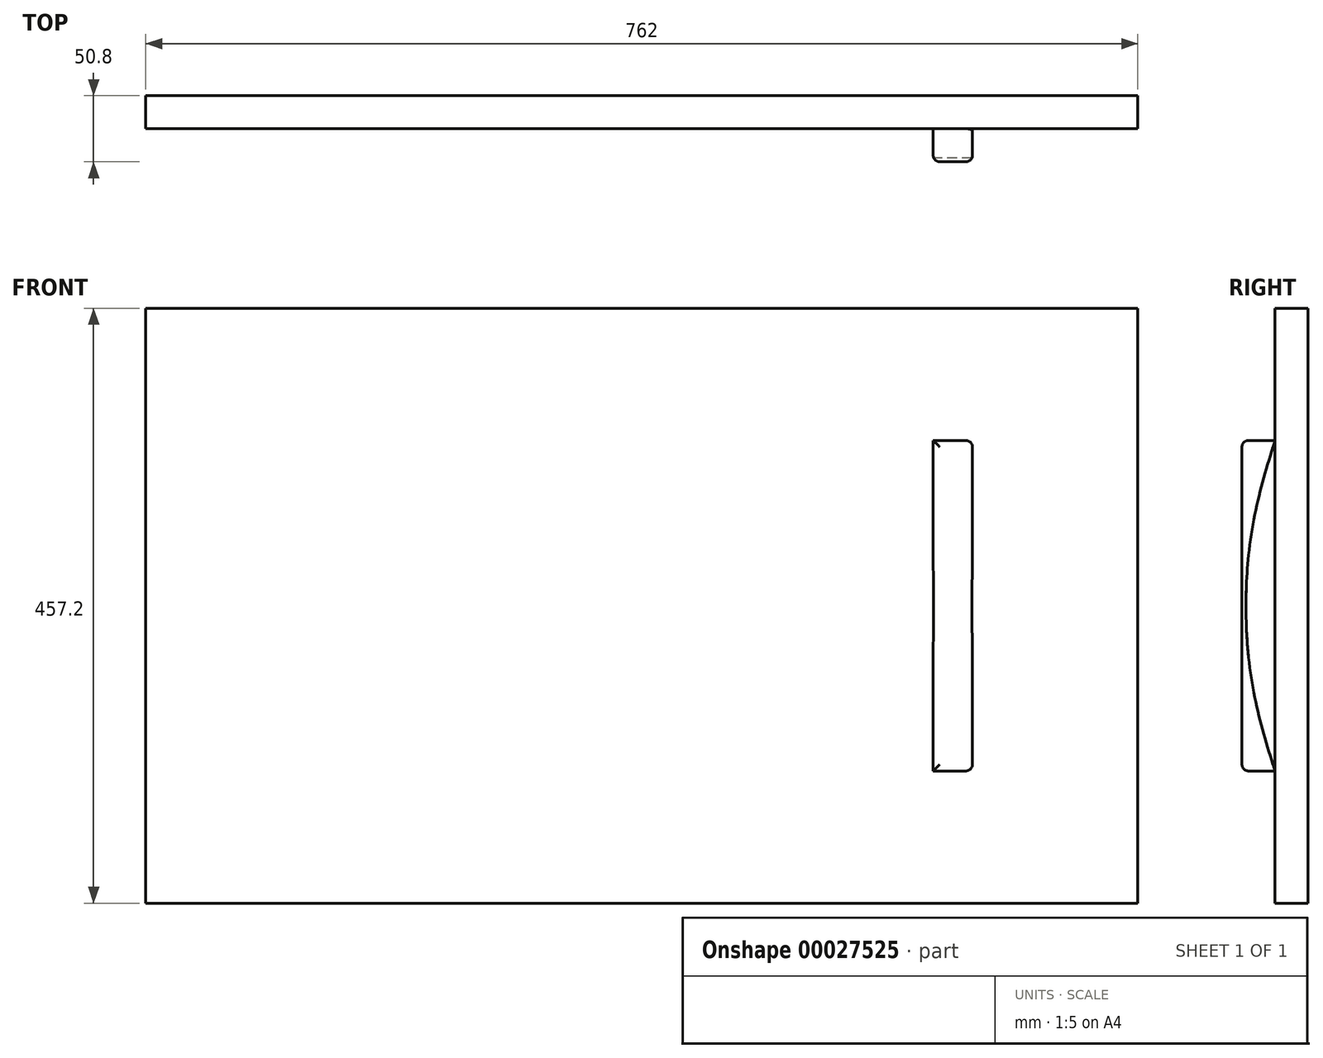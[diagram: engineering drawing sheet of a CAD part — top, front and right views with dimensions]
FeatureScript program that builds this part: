
annotation { "Feature Type Name" : "Feature", "Feature Type Description" : "" }
export const myFeature = defineFeature(function(context is Context, id is Id, definition is map)
    precondition{}
    {
        {
            var Q0;
            Q0=qCreatedBy(makeId("Front.planeOp"),FACE);
            var sketch = newSketch(context, id + "F0", { "sketchPlane" : qUnion([Q0])});
            skLineSegment(sketch, "E0.bottom", {"start": v(-381, 158.23) * mm, "end": v(381, 158.23) * mm});
            skLineSegment(sketch, "E0.top", {"start": v(-381, -298.97) * mm, "end": v(381, -298.97) * mm});
            skLineSegment(sketch, "E0.left", {"start": v(-381, 158.23) * mm, "end": v(-381, -298.97) * mm});
            skLineSegment(sketch, "E0.right", {"start": v(381, 158.23) * mm, "end": v(381, -298.97) * mm});
            skLineSegment(sketch, "E1", {"start": v(-430.92, -70.37) * mm, "end": v(506.87, -70.37) * mm, "construction": true});
            skLineSegment(sketch, "E2.bottom", {"start": v(223.82, 56.63) * mm, "end": v(254, 56.63) * mm});
            skLineSegment(sketch, "E2.top", {"start": v(223.82, -197.37) * mm, "end": v(254, -197.37) * mm});
            skLineSegment(sketch, "E2.left", {"start": v(223.82, 56.63) * mm, "end": v(223.82, -197.37) * mm});
            skLineSegment(sketch, "E2.right", {"start": v(254, 56.63) * mm, "end": v(254, -197.37) * mm});
            skSolve(sketch);
        }
        {
            var Q0;
            Q0=makeQuery(id+"F0.imprint","IMPRINT",FACE,{"disambiguationData":[TD([[makeQuery(id+"F0.imprint","IMPRINT",EDGE,{"derivedFrom":sQuery(id+"F0.wireOp",EDGE,"E2.bottom")}),-1.0]])]});
            extrude(context, id + "F1", {"entities" : qUnion([Q0]), "depth" : 50.8 * mm});
        }
        {
            var Q0;
            Q0 = qSketchRegion(id + "F0", true);
            extrude(context, id + "F2", {"entities" : qUnion([Q0]), "operationType" : NewBodyOperationType.ADD, "depth" : 25.4 * mm});
        }
        {
            var Q0;
            Q0=makeQuery(id+"F1.opExtrude","SWEPT_FACE",FACE,{"disambiguationData":[OSD([sQuery(id+"F0.wireOp",EDGE,"E2.right")])]});
            var sketch = newSketch(context, id + "F3", { "sketchPlane" : qUnion([Q0])});
            skLineSegment(sketch, "E3", {"start": v(-25.4, 56.63) * mm, "end": v(-25.4, -197.37) * mm});
            skFitSpline(sketch, "E4", {"points": [v(-25.4, 56.63) * mm, v(-44.3, -19.96) * mm, v(-44.3, -121.56) * mm, v(-25.4, -197.37) * mm], "startDerivative": vector(-70.1, -226.7) * mm, "endDerivative": vector(70.46, -225.23) * mm});
            skSolve(sketch);
        }
        {
            var Q0;
            Q0=makeQuery(id+"F3.imprint","IMPRINT",FACE,{"disambiguationData":[TD([[makeQuery(id+"F3.imprint","IMPRINT",EDGE,{"derivedFrom":sQuery(id+"F3.wireOp",EDGE,"392769a1-0da2-420d-8c07-b7950d6b351a")}),1.0]])]});
            var Q1;
            Q1=makeQuery(id+"F3.imprint","IMPRINT",FACE,{"disambiguationData":[TD([[makeQuery(id+"F3.imprint","IMPRINT",EDGE,{"derivedFrom":sQuery(id+"F3.wireOp",EDGE,"E3")}),-1.0]])]});
            extrude(context, id + "F4", {"entities" : qUnion([Q0, Q1]), "operationType" : NewBodyOperationType.REMOVE, "endBound" : BoundingType.THROUGH_ALL, "oppositeDirection" : true, "depth" : 25.4 * mm});
        }
        {
            var Q0;
            Q0=makeQuery(id+"F1.opExtrude","SWEPT_EDGE",EDGE,{"disambiguationData":[OSD([sQuery(id+"F0.wireOp",EDGE,"E2.bottom"),sQuery(id+"F0.wireOp",EDGE,"E2.right")])]});
            var Q1;
            Q1=makeQuery(id+"F1.opExtrude","CAP_EDGE",EDGE,{"disambiguationData":[OSD([sQuery(id+"F0.wireOp",EDGE,"E2.right")])],"isStart":false});
            var Q2;
            Q2=makeQuery(id+"F1.opExtrude","CAP_EDGE",EDGE,{"disambiguationData":[OSD([sQuery(id+"F0.wireOp",EDGE,"E2.left")])],"isStart":false});
            var Q3;
            Q3=makeQuery(id+"F1.opExtrude","CAP_EDGE",EDGE,{"disambiguationData":[OSD([sQuery(id+"F0.wireOp",EDGE,"E2.bottom")])],"isStart":false});
            var Q4;
            Q4=makeQuery(id+"F1.opExtrude","CAP_EDGE",EDGE,{"disambiguationData":[OSD([sQuery(id+"F0.wireOp",EDGE,"E2.top")])],"isStart":false});
            var Q5;
            Q5=makeQuery(id+"F1.opExtrude","SWEPT_EDGE",EDGE,{"disambiguationData":[OSD([sQuery(id+"F0.wireOp",EDGE,"E2.top"),sQuery(id+"F0.wireOp",EDGE,"E2.right")])]});
            fillet(context, id + "F5", {"entities" : qUnion([Q0, Q1, Q2, Q3, Q4, Q5]), "radius" : 5.08 * mm, "tangentPropagation" : true, "allowEdgeOverflow" : false});
        }
    });
